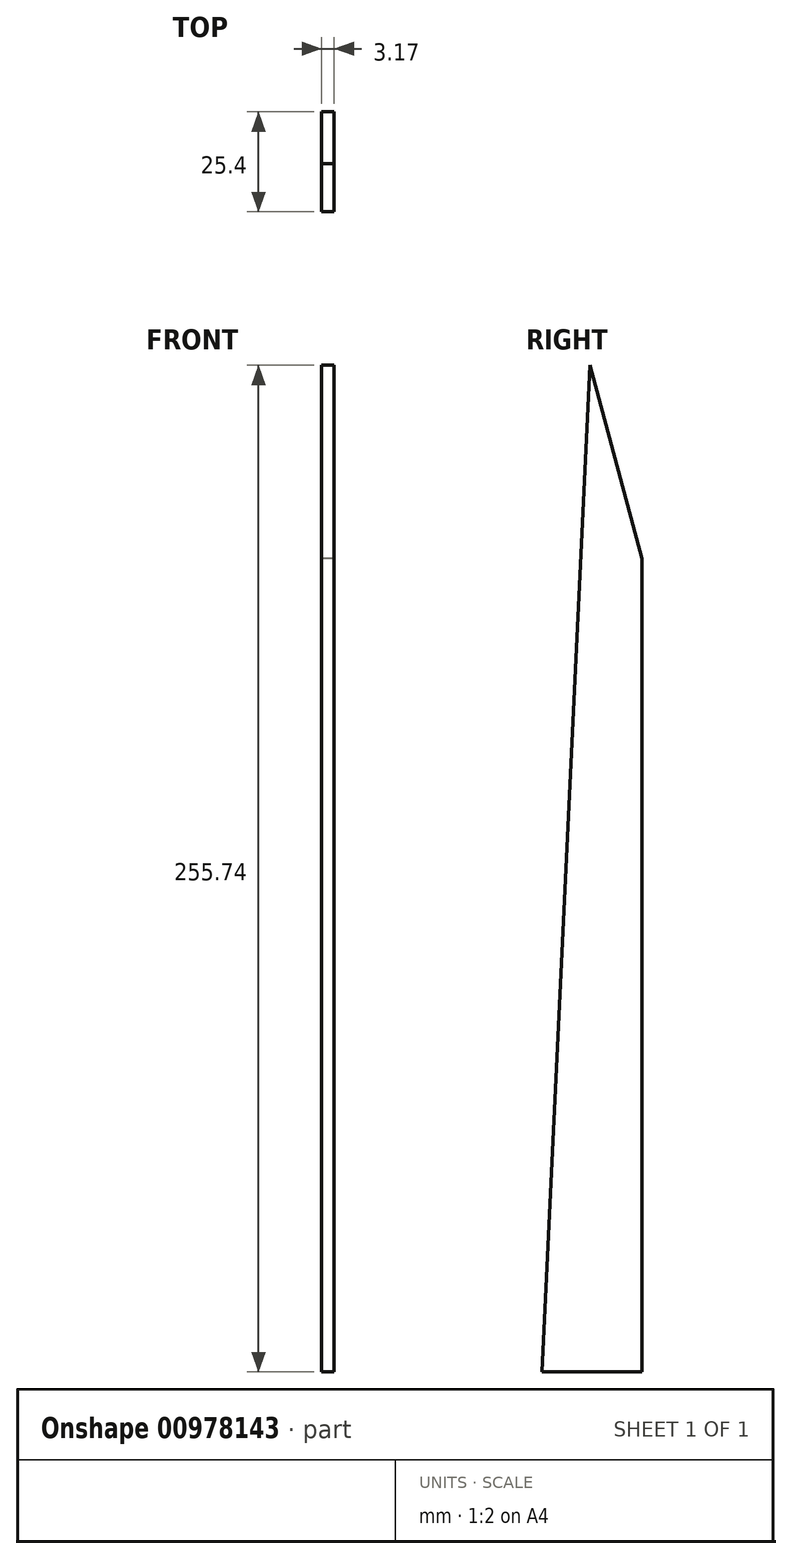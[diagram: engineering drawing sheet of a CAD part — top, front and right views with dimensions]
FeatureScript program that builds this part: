
annotation { "Feature Type Name" : "Feature", "Feature Type Description" : "" }
export const myFeature = defineFeature(function(context is Context, id is Id, definition is map)
    precondition{}
    {
        {
            var Q0;
            Q0=qCreatedBy(makeId("Right.planeOp"),FACE);
            var sketch = newSketch(context, id + "F0", { "sketchPlane" : qUnion([Q0])});
            skLineSegment(sketch, "E0.left", {"start": v(6.57, -127.87) * mm, "end": v(6.57, 78.8) * mm});
            skPoint(sketch, "E0.middle", {"position": v(0, 0) * mm});
            skLineSegment(sketch, "E1", {"start": v(-6.57, 127.87) * mm, "end": v(6.57, 78.8) * mm});
            skPoint(sketch, "E2.orphan", {"position": v(6.57, 142.59) * mm});
            skLineSegment(sketch, "E3", {"start": v(6.57, -127.87) * mm, "end": v(-18.83, -127.87) * mm});
            skLineSegment(sketch, "E4", {"start": v(-18.83, -127.87) * mm, "end": v(-6.57, 127.87) * mm});
            skSolve(sketch);
        }
        {
            var Q0;
            Q0=makeQuery(id+"F0.imprint","IMPRINT",FACE,{"disambiguationData":[TD([[makeQuery(id+"F0.imprint","IMPRINT",EDGE,{"derivedFrom":sQuery(id+"F0.wireOp",EDGE,"E0.left")}),1.0]])]});
            extrude(context, id + "F1", {"entities" : qUnion([Q0]), "depth" : 3.17 * mm, "offsetDistance" : 25.4 * mm});
        }
    });
